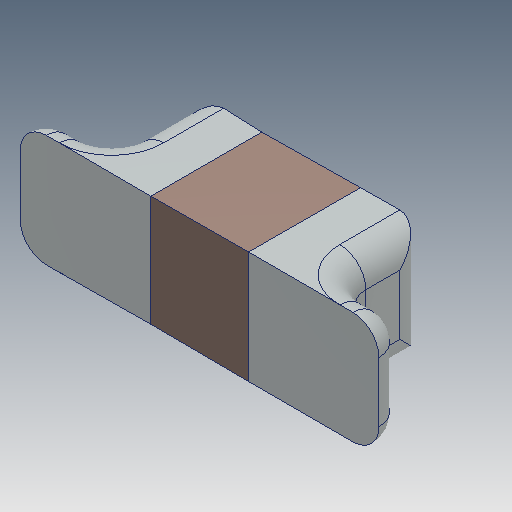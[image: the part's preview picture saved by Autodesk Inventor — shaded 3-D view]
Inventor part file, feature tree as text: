
AUTODESK INVENTOR PART (.ipt)
format: ipt  version: 2018 (Build 220112000, 112)  size: 144,896 bytes
history: native  units: mm
features: mirror x1
ambient origin geometry x8: Origin, YZ Plane, XZ Plane, XY Plane, X Axis, Y Axis, Z Axis, Center Point
bodies: Volumenkörper1 (feature_tree)
feature tree (1):
  mirror  "Mirror1"
